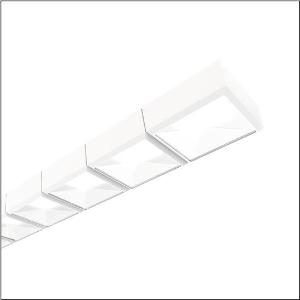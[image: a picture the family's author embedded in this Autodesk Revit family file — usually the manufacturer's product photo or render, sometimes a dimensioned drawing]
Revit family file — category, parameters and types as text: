
# Revit family: scriptus_r__11_5mz313d04wa_45ce
name_source: partatom
category: Lighting Fixtures
units: mm (PartAtom-declared; Revit-internal decimal feet)

## family parameters
Cut with Voids When Loaded = No
Host = Face
Light Source = No
Part Type = Normal
Room Calculation Point = No
Round Connector Dimension = Use Diameter
Shared = No

## types (1)
- Scriptus® 11 (1 x LED 4000K / CRI = 80 (unbekannt), 2660 lm / 4010 lm, 4000K)
    Apparent Load = 99 VA
    CIE Flux Codes = - - - 0 100 / 82 95 99 100 100
    Color Rendering = 80
    Color Temperature = 4000K
    Default Elevation = 1800 mm
    Description = Scriptus® 11, office luminaire, primary optical cover: lenses, CAT 2 (L<= 3000cd/m²), light emission: direct/indirect distribution, primary light characteristic: symmetric, installation type: suspended mounting, LED, rated luminous flux: 13.330lm, luminous efficacy: 134lm/W, light colour: 840, colour temperature: 4000K, control gear: ECG DALI, with terminal, 5-pole, mains connection: 230V, AC, 50Hz, rated input power: 99W, LED, control gear: ECG DALI, housing, luminaire housing, of aluminium, traffic white (RAL 9016), length: 2.648mm, width: 114mm, height: 57mm, protection rating (complete): IP20, insulation class (complete): insulation class I (protective earthing), certification: CE, ENEC, VDE, protection symbol: F, permissible operating ambient temperature: 0..+35°C, standard: EN 50419, packaging unit: 1 piece
    Height = 57 mm
    Lamp = 1 x LED 4000K / CRI >= 80 (unbekannt)
    Lamp Light Flux = 2660 lm / 4010 lm
    Lamp count = 1
    Length = 2648 mm
    Luminous efficacy = 134 lm/W
    Manufacturer = Siteco
    ModVariant = No
    Model = 5MZ313D04WA
    Mounting Place = Ceiling
    Mounting Type = Pendant
    Number of Poles = 1
    OnlyDefault = Yes
    Power Factor = 1
    Product Name = Scriptus® 11
    Product group = office luminaire | ceiling pendant
    ProductGroupID = 902
    Protection Class = Protection class I
    Protection Degree = IP 20
    RLX_Detail_Level = 1
    RLX_Emergency_Light_Flux = 0 lm
    RLX_Emergency_Type = 0
    RLX_Emergency_Type_DB = No
    RlxData = <blob elided: 31609 chars, md5=73ed8910>
    Socket = socket
    Standby Power = 0 W
    System Light Flux = 13340 lm
    System Power = 99 W
    Type Comments = Product without accessories
    Type Image = l_1004839.jpg
    URL = http://relux.com
    VarID = ---
    Voltage = 0 V
    Weight = 0.00 kg
    Width = 114 mm

## geometry (parser evidence)
native form markers: Blend x4, Sweep x18
no freeform markers — native parametric forms only
